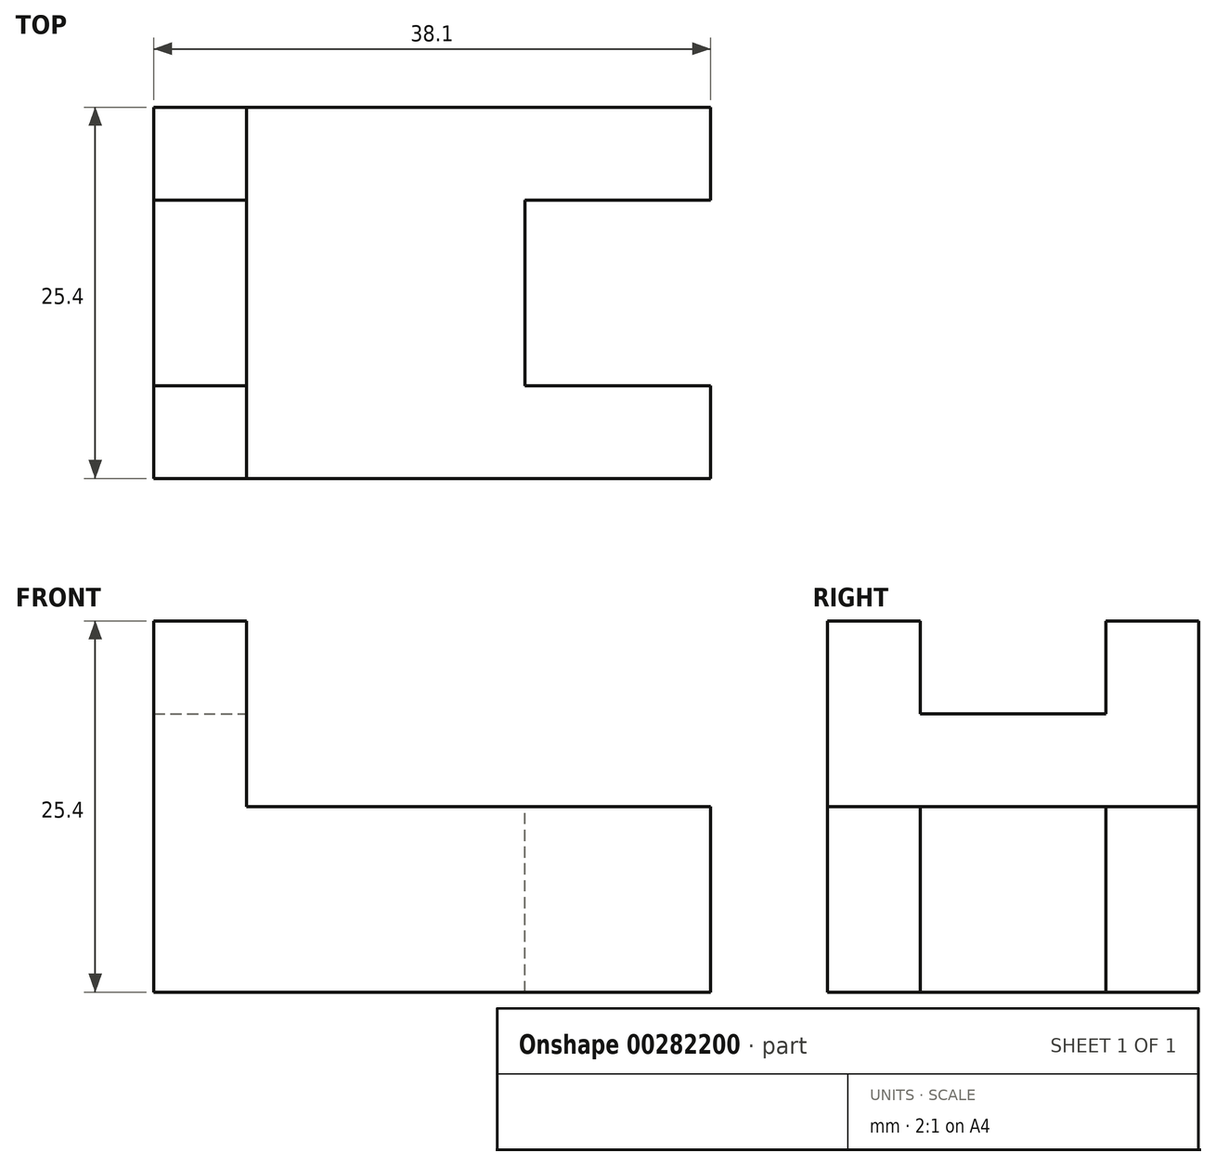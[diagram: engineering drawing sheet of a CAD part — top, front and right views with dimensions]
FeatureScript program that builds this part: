
annotation { "Feature Type Name" : "Feature", "Feature Type Description" : "" }
export const myFeature = defineFeature(function(context is Context, id is Id, definition is map)
    precondition{}
    {
        {
            var Q0;
            Q0=qCreatedBy(makeId("Top.planeOp"),FACE);
            var sketch = newSketch(context, id + "F0", { "sketchPlane" : qUnion([Q0])});
            skLineSegment(sketch, "E0.bottom", {"start": v(0, 0) * mm, "end": v(38.1, 0) * mm});
            skLineSegment(sketch, "E0.top", {"start": v(0, -25.4) * mm, "end": v(38.1, -25.4) * mm});
            skLineSegment(sketch, "E0.left", {"start": v(0, 0) * mm, "end": v(0, -25.4) * mm});
            skLineSegment(sketch, "E0.right", {"start": v(38.1, 0) * mm, "end": v(38.1, -25.4) * mm});
            skSolve(sketch);
        }
        {
            var Q0;
            Q0 = qSketchRegion(id + "F0", true);
            extrude(context, id + "F1", {"entities" : qUnion([Q0]), "depth" : 12.7 * mm});
        }
        {
            var Q0;
            Q0=makeQuery(id+"F1.opExtrude","CAP_FACE",FACE,{"disambiguationData":[OSD([sQuery(id+"F0.wireOp",EDGE,"E0.bottom"),sQuery(id+"F0.wireOp",EDGE,"E0.top"),sQuery(id+"F0.wireOp",EDGE,"E0.left"),sQuery(id+"F0.wireOp",EDGE,"E0.right")])],"isStart":false});
            var sketch = newSketch(context, id + "F2", { "sketchPlane" : qUnion([Q0])});
            skLineSegment(sketch, "E1.bottom", {"start": v(0, 0) * mm, "end": v(6.35, 0) * mm});
            skLineSegment(sketch, "E1.top", {"start": v(0, -25.4) * mm, "end": v(6.35, -25.4) * mm});
            skLineSegment(sketch, "E1.left", {"start": v(0, 0) * mm, "end": v(0, -25.4) * mm});
            skLineSegment(sketch, "E1.right", {"start": v(6.35, 0) * mm, "end": v(6.35, -25.4) * mm});
            skSolve(sketch);
        }
        {
            var Q0;
            Q0 = qSketchRegion(id + "F2", true);
            extrude(context, id + "F3", {"entities" : qUnion([Q0]), "operationType" : NewBodyOperationType.ADD, "depth" : 12.7 * mm});
        }
        {
            var Q0;
            Q0=makeQuery(id+"F1.opExtrude","CAP_FACE",FACE,{"disambiguationData":[OSD([sQuery(id+"F0.wireOp",EDGE,"E0.bottom"),sQuery(id+"F0.wireOp",EDGE,"E0.top"),sQuery(id+"F0.wireOp",EDGE,"E0.left"),sQuery(id+"F0.wireOp",EDGE,"E0.right")])],"isStart":false});
            var sketch = newSketch(context, id + "F4", { "sketchPlane" : qUnion([Q0])});
            skLineSegment(sketch, "E2.bottom", {"start": v(38.1, -6.35) * mm, "end": v(25.4, -6.35) * mm});
            skLineSegment(sketch, "E2.top", {"start": v(38.1, -19.05) * mm, "end": v(25.4, -19.05) * mm});
            skLineSegment(sketch, "E2.left", {"start": v(38.1, -6.35) * mm, "end": v(38.1, -19.05) * mm});
            skLineSegment(sketch, "E2.right", {"start": v(25.4, -6.35) * mm, "end": v(25.4, -19.05) * mm});
            skSolve(sketch);
        }
        {
            var Q0;
            Q0 = qSketchRegion(id + "F4", true);
            extrude(context, id + "F5", {"entities" : qUnion([Q0]), "operationType" : NewBodyOperationType.REMOVE, "oppositeDirection" : true, "depth" : 12.7 * mm});
        }
        {
            var Q0;
            Q0=makeQuery(id+"F3.opExtrude","CAP_FACE",FACE,{"disambiguationData":[OSD([sQuery(id+"F2.wireOp",EDGE,"E1.bottom"),sQuery(id+"F2.wireOp",EDGE,"E1.top"),sQuery(id+"F2.wireOp",EDGE,"E1.left"),sQuery(id+"F2.wireOp",EDGE,"E1.right")])],"isStart":false});
            var sketch = newSketch(context, id + "F6", { "sketchPlane" : qUnion([Q0])});
            skLineSegment(sketch, "E3.bottom", {"start": v(0, -6.35) * mm, "end": v(6.35, -6.35) * mm});
            skLineSegment(sketch, "E3.top", {"start": v(0, -19.05) * mm, "end": v(6.35, -19.05) * mm});
            skLineSegment(sketch, "E3.left", {"start": v(0, -6.35) * mm, "end": v(0, -19.05) * mm});
            skLineSegment(sketch, "E3.right", {"start": v(6.35, -6.35) * mm, "end": v(6.35, -19.05) * mm});
            skSolve(sketch);
        }
        {
            var Q0;
            Q0 = qSketchRegion(id + "F6", true);
            extrude(context, id + "F7", {"entities" : qUnion([Q0]), "operationType" : NewBodyOperationType.REMOVE, "oppositeDirection" : true, "depth" : 6.35 * mm});
        }
    });
